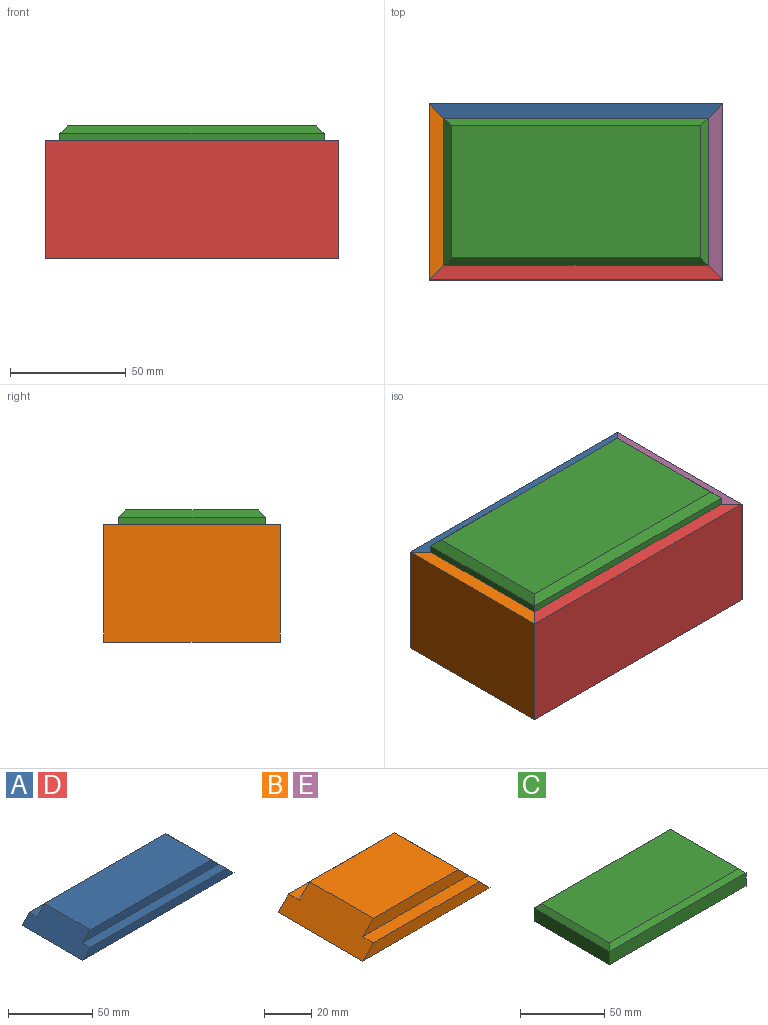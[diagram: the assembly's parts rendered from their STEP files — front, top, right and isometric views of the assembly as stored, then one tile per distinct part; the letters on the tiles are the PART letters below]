
ASSEMBLY  parts=5 mates=6
PART A: 10 faces, bbox 127x50.8x12.7 mm
  f0: plane 101.6x38.1mm, normal (0,0,1), area 3871mm2, adj f1,f3,f6,f9
  f1: plane 50.8x12.7mm, normal (-0.71,0,0.71), area 798.3mm2, adj f0,f2,f4,f5,f6,f7,f8,f9
  f2: plane 127x50.8mm, normal (0,0,-1), area 6451.6mm2, adj f1,f3,f4,f5
  f3: plane 50.8x12.7mm, normal (0.71,0,0.71), area 798.3mm2, adj f0,f2,f4,f5,f6,f7,f8,f9
  f4: plane 127x6.35mm, normal (0,-1,0), area 766.1mm2, adj f1,f2,f3,f8
  f5: plane 127x6.35mm, normal (0,1,0), area 766.1mm2, adj f1,f2,f3,f7
  f6: plane 114.3x6.35mm, normal (0,1,0), area 685.5mm2, adj f0,f1,f3,f7
  f7: plane 114.3x6.35mm, normal (0,0,1), area 725.8mm2, adj f1,f3,f5,f6
  f8: plane 114.3x6.35mm, normal (0,0,1), area 725.8mm2, adj f1,f3,f4,f9
  f9: plane 114.3x6.35mm, normal (0,-1,0), area 685.5mm2, adj f0,f1,f3,f8
PART B: 10 faces, bbox 76.2x50.8x12.7 mm
  f0: plane 50.8x38.1mm, normal (0,0,1), area 1935.5mm2, adj f1,f2,f6,f9
  f1: plane 50.8x12.7mm, normal (-0.71,0,0.71), area 798.3mm2, adj f0,f3,f4,f5,f6,f7,f8,f9
  f2: plane 50.8x12.7mm, normal (0.71,0,0.71), area 798.3mm2, adj f0,f3,f4,f5,f6,f7,f8,f9
  f3: plane 76.2x6.35mm, normal (0,-1,0), area 443.5mm2, adj f1,f2,f5,f8
  f4: plane 76.2x6.35mm, normal (0,1,0), area 443.5mm2, adj f1,f2,f5,f7
  f5: plane 76.2x50.8mm, normal (0,0,-1), area 3871mm2, adj f1,f2,f3,f4
  f6: plane 63.5x6.35mm, normal (0,1,0), area 362.9mm2, adj f0,f1,f2,f7
  f7: plane 63.5x6.35mm, normal (0,0,1), area 403.2mm2, adj f1,f2,f4,f6
  f8: plane 63.5x6.35mm, normal (0,0,1), area 403.2mm2, adj f1,f2,f3,f9
  f9: plane 63.5x6.35mm, normal (0,-1,0), area 362.9mm2, adj f0,f1,f2,f8
PART C: 10 faces, bbox 114.3x63.5x12.7 mm
  f0: plane 63.5x9.53mm, normal (1,0,0), area 604.8mm2, adj f1,f3,f5,f6
  f1: plane 114.3x9.53mm, normal (0,1,0), area 1088.7mm2, adj f0,f2,f5,f7
  f2: plane 63.5x9.53mm, normal (-1,0,0), area 604.8mm2, adj f1,f3,f5,f9
  f3: plane 114.3x9.53mm, normal (0,-1,0), area 1088.7mm2, adj f0,f2,f5,f8
  f4: plane 107.95x57.15mm, normal (0,0,1), area 6169.3mm2, adj f6,f7,f8,f9
  f5: plane 114.3x63.5mm, normal (0,0,-1), area 7258.1mm2, adj f0,f1,f2,f3
  f6: plane 63.5x3.18mm, normal (0.71,0,0.71), area 270.9mm2, adj f0,f4,f7,f8
  f7: plane 114.3x3.18mm, normal (0,0.71,0.71), area 499mm2, adj f1,f4,f6,f9
  f8: plane 114.3x3.18mm, normal (0,-0.71,0.71), area 499mm2, adj f3,f4,f6,f9
  f9: plane 63.5x3.18mm, normal (-0.71,0,0.71), area 270.9mm2, adj f2,f4,f7,f8
PART D: same geometry as A
PART E: same geometry as B
PLACE A rot(axis=(1,0,0),90deg) t=(142.27,114.51,-56.22)mm
PLACE B rot(axis=(-0.58,0.58,-0.58),120deg) t=(78.77,76.41,-56.22)mm
PLACE C t=(142.27,76.41,-37.17)mm
PLACE D rot(axis=(-1,0,0),90deg) t=(142.27,38.31,-56.22)mm fixed
PLACE E rot(axis=(0.58,-0.58,-0.58),120deg) t=(205.77,76.41,-56.22)mm
MATE fastened D.f1 <-> B.f2  axis (-0.71,0.71,0) through (84.67,44.2,-56.22)mm
MATE fastened A.f3 <-> E.f1  axis (0.71,-0.71,0) through (199.87,108.61,-56.22)mm
MATE fastened D.f3 <-> E.f2  axis (0.71,0.71,0) through (199.87,44.2,-56.22)mm
MATE planar C.f3 <-> D.f8  axis (0,-1,0) through (142.27,44.66,-32.41)mm
MATE planar C.f5 <-> A.f6  axis (0,0,-1) through (142.27,76.41,-37.17)mm
MATE planar C.f2 <-> B.f8  axis (-1,0,0) through (85.12,76.41,-32.41)mm
